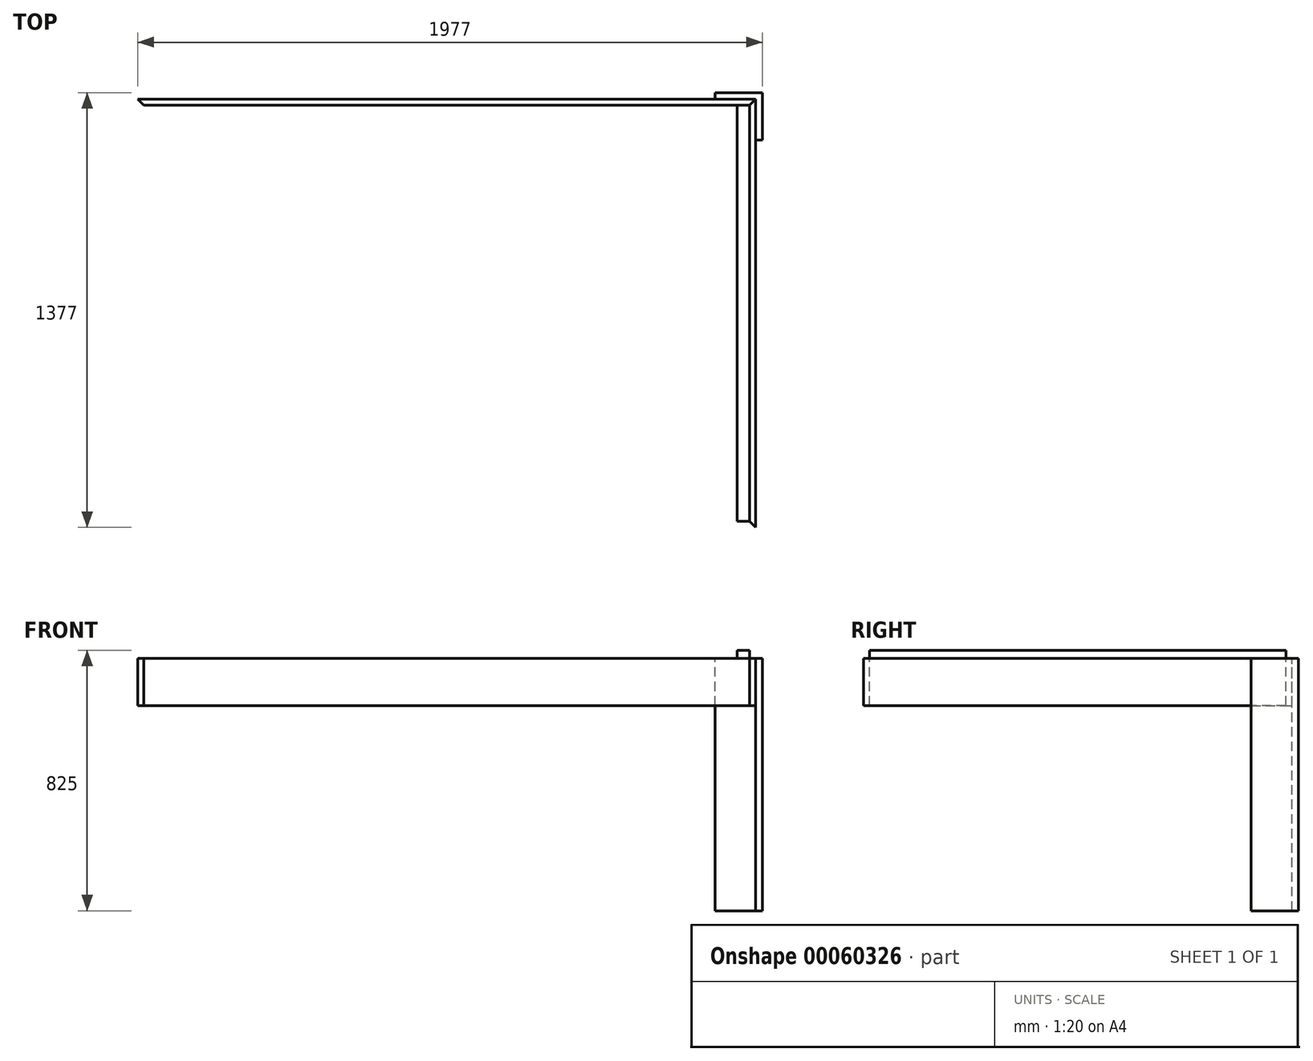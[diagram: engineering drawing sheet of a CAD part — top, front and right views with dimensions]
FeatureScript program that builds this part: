
annotation { "Feature Type Name" : "Feature", "Feature Type Description" : "" }
export const myFeature = defineFeature(function(context is Context, id is Id, definition is map)
    precondition{}
    {
        {
            var Q0;
            Q0=qCreatedBy(makeId("Top.planeOp"),FACE);
            var sketch = newSketch(context, id + "F0", { "sketchPlane" : qUnion([Q0])});
            skLineSegment(sketch, "E0", {"start": v(-768.93, 880.68) * mm, "end": v(1187.07, 880.68) * mm});
            skLineSegment(sketch, "E1", {"start": v(1168.07, 861.68) * mm, "end": v(-749.93, 861.68) * mm});
            skLineSegment(sketch, "E2", {"start": v(-749.93, 861.68) * mm, "end": v(-768.93, 880.68) * mm});
            skLineSegment(sketch, "E3", {"start": v(1187.07, 880.68) * mm, "end": v(1168.07, 861.68) * mm});
            skLineSegment(sketch, "E4", {"start": v(1187.07, -475.32) * mm, "end": v(1187.07, 880.68) * mm});
            skLineSegment(sketch, "E5", {"start": v(1168.07, -456.32) * mm, "end": v(1187.07, -475.32) * mm});
            skLineSegment(sketch, "E6", {"start": v(1168.07, 861.68) * mm, "end": v(1168.07, -456.32) * mm});
            skLineSegment(sketch, "E7", {"start": v(1058.07, 880.68) * mm, "end": v(1058.07, 901.68) * mm});
            skLineSegment(sketch, "E8", {"start": v(1058.07, 901.68) * mm, "end": v(1208.07, 901.68) * mm});
            skLineSegment(sketch, "E9", {"start": v(1208.07, 901.68) * mm, "end": v(1187.07, 880.68) * mm});
            skLineSegment(sketch, "E10", {"start": v(1208.07, 901.68) * mm, "end": v(1208.07, 751.68) * mm});
            skLineSegment(sketch, "E11", {"start": v(1208.07, 751.68) * mm, "end": v(1187.07, 751.68) * mm});
            skLineSegment(sketch, "E12", {"start": v(1128.07, 861.68) * mm, "end": v(1128.07, -456.32) * mm});
            skLineSegment(sketch, "E13", {"start": v(1128.07, -456.32) * mm, "end": v(1168.07, -456.32) * mm});
            skSolve(sketch);
        }
        {
            var Q0;
            {var subQ2=sQuery(id+"F0.wireOp",EDGE,"E3");Q0=makeQuery(id+"F0.imprint","IMPRINT",FACE,{"disambiguationData":[TD([[makeQuery(id+"F0.imprint","IMPRINT",EDGE,{"derivedFrom":subQ2}),1.0]])]});}
            extrude(context, id + "F1", {"entities" : qUnion([Q0]), "oppositeDirection" : true, "depth" : 150 * mm});
        }
        {
            var Q0;
            Q0=makeQuery(id+"F0.imprint","IMPRINT",FACE,{"disambiguationData":[TD([[makeQuery(id+"F0.imprint","IMPRINT",EDGE,{"derivedFrom":sQuery(id+"F0.wireOp",EDGE,"E1")}),-1.0]])]});
            var Q1;
            Q1=sQuery(id+"F0.wireOp",EDGE,"E1");
            var Q2;
            Q2=sQuery(id+"F0.wireOp",EDGE,"E0");
            extrude(context, id + "F2", {"entities" : qUnion([Q0]), "surfaceEntities" : qUnion([Q1, Q2]), "oppositeDirection" : true, "depth" : 150 * mm});
        }
        {
            var Q0;
            {var subQ2=sQuery(id+"F0.wireOp",EDGE,"E7");Q0=makeQuery(id+"F0.imprint","IMPRINT",FACE,{"disambiguationData":[TD([[makeQuery(id+"F0.imprint","IMPRINT",EDGE,{"derivedFrom":subQ2}),-1.0]])]});}
            var Q1;
            {var subQ0=sQuery(id+"F0.wireOp",EDGE,"E9");Q1=makeQuery(id+"F0.imprint","IMPRINT",FACE,{"disambiguationData":[TD([[makeQuery(id+"F0.imprint","IMPRINT",EDGE,{"derivedFrom":subQ0}),1.0]])]});}
            extrude(context, id + "F3", {"entities" : qUnion([Q0, Q1]), "oppositeDirection" : true, "depth" : 800 * mm});
        }
        {
            var Q0;
            {var subQ0=sQuery(id+"F0.wireOp",EDGE,"E6");Q0=makeQuery(id+"F0.imprint","IMPRINT",FACE,{"disambiguationData":[TD([[makeQuery(id+"F0.imprint","IMPRINT",EDGE,{"derivedFrom":subQ0}),-1.0]])]});}
            extrude(context, id + "F4", {"entities" : qUnion([Q0]), "depth" : 25 * mm});
        }
    });
